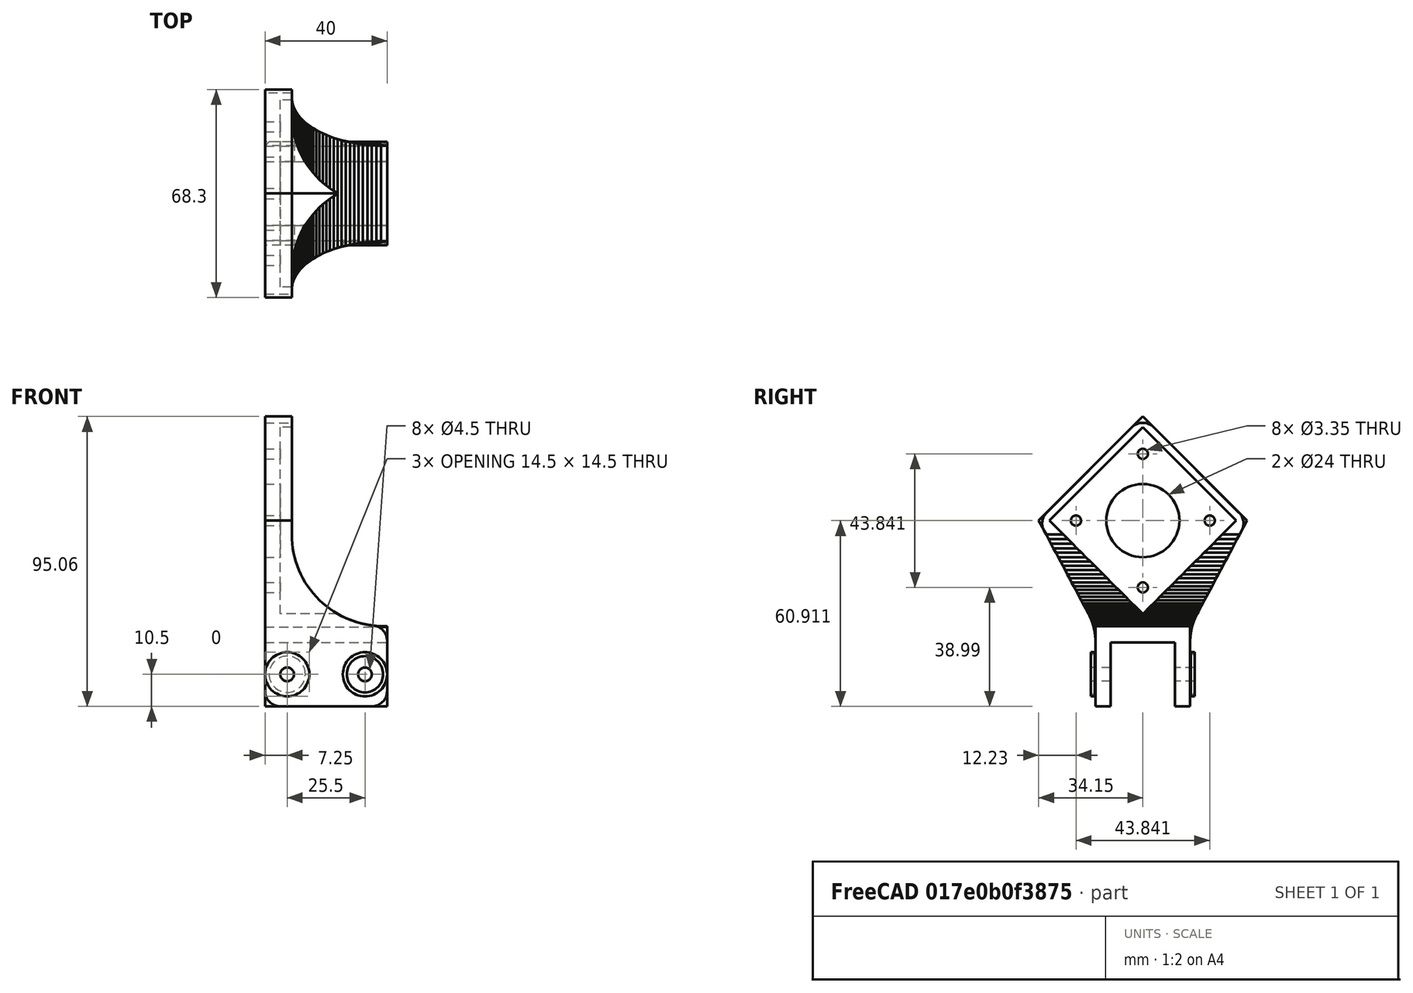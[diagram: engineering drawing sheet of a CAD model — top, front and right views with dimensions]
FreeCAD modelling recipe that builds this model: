
FCSTD DOCUMENT  (FreeCAD 0.19R24267 +99 (Git))
Label: monturaExtrusor
License: All rights reserved
LicenseURL: http://en.wikipedia.org/wiki/All_rights_reserved
objects: Part::Fillet×10, Part::Cylinder×7, Part::Fuse×7, Part::Box×6, Part::Part2DObjectPython×5, Part::Cut×3, Part::FeaturePython×3, Part::MultiFuse×3, Part::Chamfer×3, Part::Extrusion×1, Part::Refine×1
note: 49 computed .brp shape members not serialized (recipe doc carries the construction recipe); baked Part::Feature solids carry a one-line shape summary decoded from their .brp

FEATURE [Part::Box] cube
  AttacherType = Attacher::AttachEngine3D
  Height = 26
  Length = 40
  Placement = pos=(-20,-15.5,-13) rot=(0,0,1;0rad)
  Width = 31
FEATURE [Part::Box] cube001
  AttacherType = Attacher::AttachEngine3D
  Height = 21
  Length = 80
  Placement = pos=(-40,-10.5,-13) rot=(0,0,1;0rad)
  Width = 21
FEATURE [Part::Cut] difference
  Base = -> cube
  Placement = pos=(15,0,-13) rot=(0,0,1;0rad)
  Tool = -> cube001
FEATURE [Part::Cylinder] cylinder
  Angle = 360
  AttacherType = Attacher::AttachEngine3D
  Height = 6.5
  Placement = pos=(0,0,0) rot=(1,0,0;1.5708rad)
  Radius = 7.25
FEATURE [Part::Cylinder] cylinder001
  Angle = 360
  AttacherType = Attacher::AttachEngine3D
  Height = 6.5
  Placement = pos=(25.5,0,0) rot=(1,0,0;1.5708rad)
  Radius = 7.25
FEATURE [Part::Fuse] Group
  Base = -> cylinder
  Placement = pos=(2.25,-10.5,-15.5) rot=(0,0,1;0rad)
  Tool = -> cylinder001
FEATURE [Part::Cylinder] cylinder002
  Angle = 360
  AttacherType = Attacher::AttachEngine3D
  Height = 6.5
  Placement = pos=(0,0,0) rot=(1,0,0;1.5708rad)
  Radius = 7.25
FEATURE [Part::Cylinder] cylinder003
  Angle = 360
  AttacherType = Attacher::AttachEngine3D
  Height = 6.5
  Placement = pos=(25.5,0,0) rot=(1,0,0;1.5708rad)
  Radius = 7.25
FEATURE [Part::Fuse] Group001
  Base = -> cylinder002
  Placement = pos=(2.25,10.5,-15.5) rot=(1,0,0;3.14159rad)
  Tool = -> cylinder003
FEATURE [Part::Fuse] Group002
  Base = -> Group
  Tool = -> Group001
FEATURE [Part::Fuse] union
  Base = -> difference
  Tool = -> Group002
FEATURE [Part::Cylinder] cylinder004
  Angle = 360
  AttacherType = Attacher::AttachEngine3D
  Height = 1000
  Placement = pos=(0,500,0) rot=(1,0,0;1.5708rad)
  Radius = 2.25
FEATURE [Part::Cylinder] cylinder005
  Angle = 360
  AttacherType = Attacher::AttachEngine3D
  Height = 1000
  Placement = pos=(25.5,500,0) rot=(1,0,0;1.5708rad)
  Radius = 2.25
FEATURE [Part::Fuse] Group003
  Base = -> cylinder004
  Placement = pos=(2.25,0,-15.5) rot=(0,0,1;0rad)
  Tool = -> cylinder005
FEATURE [Part::Cut] difference001
  Base = -> union
  Tool = -> Group003
FEATURE [Part::Box] cube002
  AttacherType = Attacher::AttachEngine3D
  Height = 5
  Length = 40
  Placement = pos=(35,15.5,0) rot=(0,0,1;3.14159rad)
  Width = 31
FEATURE [Part::Box] cube003
  AttacherType = Attacher::AttachEngine3D
  Height = 40
  Length = 48.3
  Placement = pos=(35,-34.1533,34.9106) rot=(-0.357407,-0.862856,0.357407;1.71777rad)
  Width = 48.3
FEATURE [Part::FeaturePython] hull  # WARN: FeaturePython — macro-defined, semantics opaque (R4)
  Arguments = []
  Children = -> [cube002,cube003]
  Operation = hull
FEATURE [Part::Box] cube004
  AttacherType = Attacher::AttachEngine3D
  Height = 1000
  Length = 43.3
  Placement = pos=(1000,-30.6177,34.9106) rot=(-0.357407,-0.862856,0.357407;1.71777rad)
  Width = 43.3
FEATURE [Part::Part2DObjectPython] circle  # Draft 2D object (typed FeaturePython)
  Area = 452.389
  FirstAngle = 0
  LastAngle = 0
  MakeFace = true
  Radius = 12
FEATURE [Part::Part2DObjectPython] circle001  # Draft 2D object (typed FeaturePython)
  Area = 8.81413
  FirstAngle = 0
  LastAngle = 0
  MakeFace = true
  Placement = pos=(15.5,15.5,0) rot=(0,0,1;0rad)
  Radius = 1.675
FEATURE [Part::Part2DObjectPython] circle002  # Draft 2D object (typed FeaturePython)
  Area = 8.81413
  FirstAngle = 0
  LastAngle = 0
  MakeFace = true
  Placement = pos=(-15.5,15.5,0) rot=(0,0,1;1.5708rad)
  Radius = 1.675
FEATURE [Part::Part2DObjectPython] circle003  # Draft 2D object (typed FeaturePython)
  Area = 8.81413
  FirstAngle = 0
  LastAngle = 0
  MakeFace = true
  Placement = pos=(-15.5,-15.5,0) rot=(0,0,1;3.14159rad)
  Radius = 1.675
FEATURE [Part::Part2DObjectPython] circle004  # Draft 2D object (typed FeaturePython)
  Area = 8.81413
  FirstAngle = 0
  LastAngle = 0
  MakeFace = true
  Placement = pos=(15.5,-15.5,0) rot=(0,0,-1;1.5708rad)
  Radius = 1.675
FEATURE [Part::MultiFuse] Group004
  Shapes = -> [circle001,circle002,circle003,circle004]
FEATURE [Part::Fuse] Group005
  Base = -> circle
  Tool = -> Group004
FEATURE [Part::FeaturePython] RefineLinearExtrude  # WARN: FeaturePython — macro-defined, semantics opaque (R4)
  Base = -> Group005
FEATURE [Part::Extrusion] LinearExtrude
  Base = -> RefineLinearExtrude
  Dir = (0,0,1000)
  DirMode = 0
  FaceMakerClass = Part::FaceMakerBullseye
  LengthFwd = 0
  LengthRev = 0
  Placement = pos=(505,0,34.9106) rot=(-0.357407,-0.862856,0.357407;1.71777rad)
  Solid = false
  Symmetric = false
FEATURE [Part::Box] cube005
  AttacherType = Attacher::AttachEngine3D
  Height = 84
  Length = 2.5
  Placement = pos=(-1.25,-500,-42) rot=(0,0,1;0rad)
  Width = 1000
FEATURE [Part::Cylinder] cylinder006
  Angle = 360
  AttacherType = Attacher::AttachEngine3D
  Height = 0.01
  Placement = pos=(0,0.005,0) rot=(1,0,0;1.5708rad)
  Radius = 30
FEATURE [Part::FeaturePython] minkowski  # WARN: FeaturePython — macro-defined, semantics opaque (R4)
  Arguments = {'convexity': '0'}
  Children = -> [cube005,cylinder006]
  Operation = minkowski
  Placement = pos=(35,0,72.3212) rot=(0,0,1;0rad)
FEATURE [Part::MultiFuse] union001
  Shapes = -> [cube004,LinearExtrude,minkowski]
FEATURE [Part::Cut] difference002
  Base = -> hull
  Tool = -> union001
FEATURE [Part::Fuse] Group006
  Base = -> difference001
  Tool = -> difference002
FEATURE [Part::MultiFuse] Fusion
  Shapes = -> [difference002,difference001]
FEATURE [Part::Refine] Fusion001
  Source = -> Fusion
FEATURE [Part::Fillet] Fillet
  Base = -> Fusion001
  Edges = 1 edges r=5: [Edge14]
FEATURE [Part::Fillet] Fillet001
  Base = -> Fillet
  Edges = 1 edges r=5: [Edge12]
FEATURE [Part::Fillet] Fillet002
  Base = -> Fillet001
  Edges = 1 edges r=5: [Edge20]
FEATURE [Part::Chamfer] Chamfer
  Base = -> Fillet002
  Edges = 1 edges r=1.3: [Edge252]
FEATURE [Part::Chamfer] Chamfer001
  Base = -> Chamfer
  Edges = 1 edges r=1.3: [Edge80]
FEATURE [Part::Chamfer] Chamfer002
  Base = -> Chamfer001
  Edges = 1 edges r=1.3: [Edge254]
FEATURE [Part::Fillet] Fillet003
  Base = -> Chamfer002
  Edges = 1 edges r=20: [Edge10]
FEATURE [Part::Fillet] Fillet004
  Base = -> Fillet003
  Edges = 1 edges r=20: [Edge99]
FEATURE [Part::Fillet] Fillet005
  Base = -> Fillet004
  Edges = 1 edges r=5: [Edge5]
FEATURE [Part::Fillet] Fillet006
  Base = -> Fillet005
  Edges = 1 edges r=5: [Edge6]
FEATURE [Part::Fillet] Fillet007
  Base = -> Fillet006
  Edges = 1 edges r=5: [Edge150]
FEATURE [Part::Fillet] Fillet008
  Base = -> Fillet007
  Edges = 1 edges r=5: [Edge23]
FEATURE [Part::Fillet] Fillet009
  Base = -> Fillet008
  Edges = 1 edges r=5: [Edge10]
